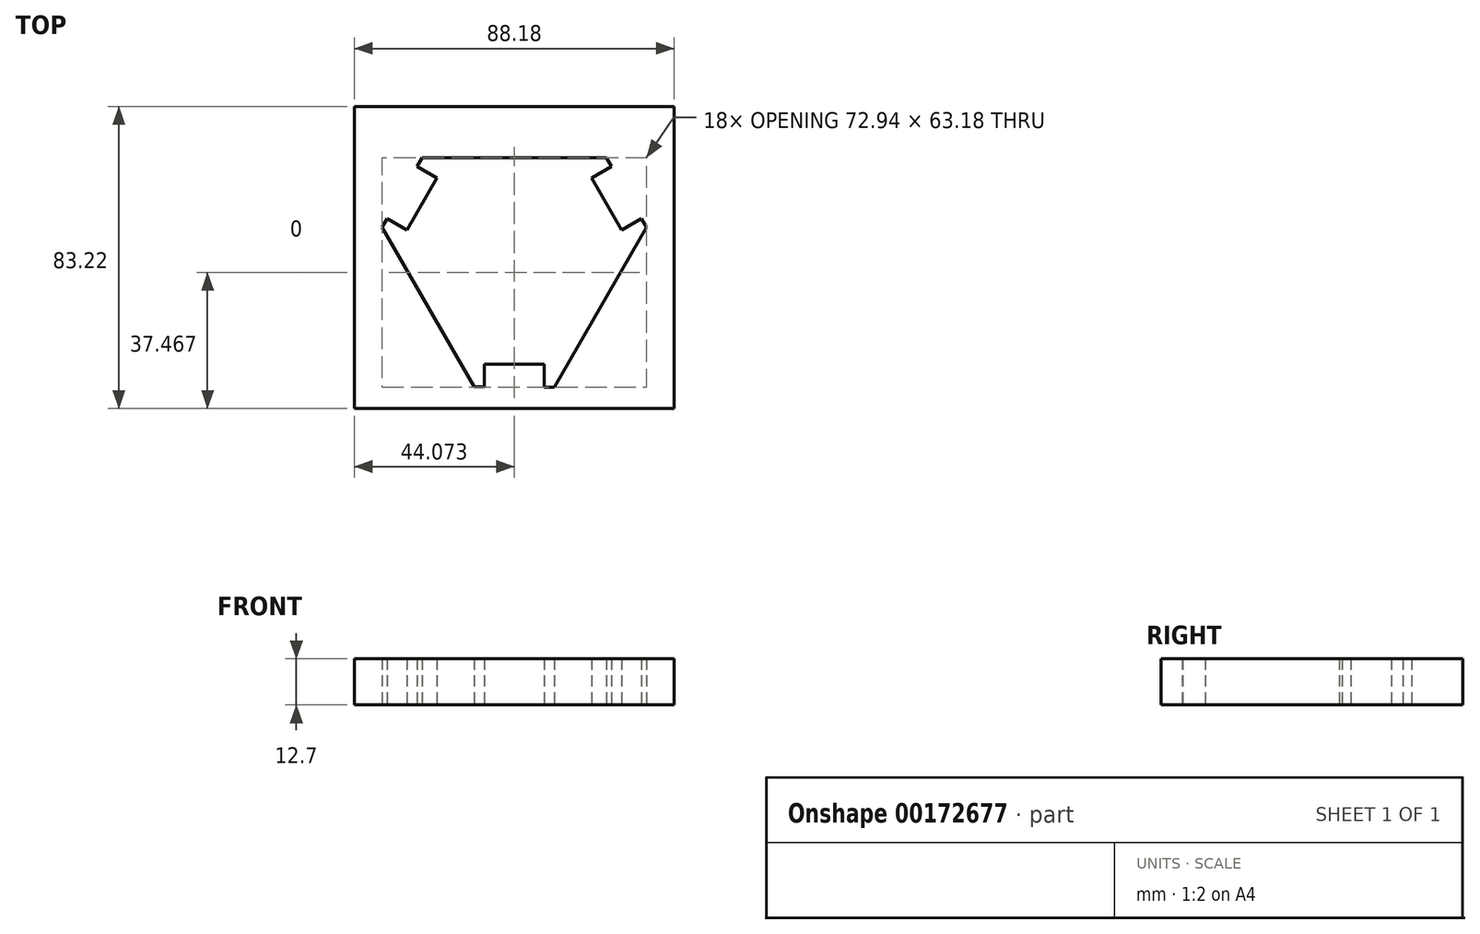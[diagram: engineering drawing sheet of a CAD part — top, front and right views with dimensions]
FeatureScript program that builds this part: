
annotation { "Feature Type Name" : "Feature", "Feature Type Description" : "" }
export const myFeature = defineFeature(function(context is Context, id is Id, definition is map)
    precondition{}
    {
        {
            var Q0;
            Q0=qCreatedBy(makeId("Top.planeOp"),FACE);
            var sketch = newSketch(context, id + "F0", { "sketchPlane" : qUnion([Q0])});
            skCircle(sketch, "E0", {"center": v(0, 0) * mm, "radius": 6.35 * mm, "construction": true});
            skLineSegment(sketch, "E1.bottom", {"start": v(-1.6, 6.15) * mm, "end": v(1.6, 6.15) * mm, "construction": true});
            skLineSegment(sketch, "E1.top", {"start": v(-1.6, 24.25) * mm, "end": v(0, 24.25) * mm, "construction": true});
            skLineSegment(sketch, "E1.left", {"start": v(-1.6, 6.15) * mm, "end": v(-1.6, 24.25) * mm, "construction": true});
            skLineSegment(sketch, "E1.right", {"start": v(1.6, 6.15) * mm, "end": v(1.6, 24.25) * mm, "construction": true});
            skLineSegment(sketch, "E2.bottom", {"start": v(-25.4, 27.45) * mm, "end": v(25.4, 27.45) * mm});
            skLineSegment(sketch, "E2.left", {"start": v(-25.4, 27.45) * mm, "end": v(-25.4, 24.25) * mm, "construction": true});
            skLineSegment(sketch, "E2.right", {"start": v(25.4, 27.45) * mm, "end": v(25.4, 24.25) * mm, "construction": true});
            skPoint(sketch, "E2.middle", {"position": v(0, 24.25) * mm});
            skLineSegment(sketch, "E3", {"start": v(-25.4, 24.25) * mm, "end": v(-1.6, 24.25) * mm, "construction": true});
            skPoint(sketch, "E4.orphan", {"position": v(-25.4, 21.05) * mm});
            skPoint(sketch, "E5.orphan", {"position": v(25.4, 21.05) * mm});
            skLineSegment(sketch, "E6.trimOffspring", {"start": v(1.6, 24.25) * mm, "end": v(25.4, 24.25) * mm, "construction": true});
            skLineSegment(sketch, "E7.1.0", {"start": v(-11.09, -35.7) * mm, "end": v(-36.49, 8.29) * mm});
            skLineSegment(sketch, "E7.1.1", {"start": v(-36.49, 8.29) * mm, "end": v(-33.71, 9.88) * mm, "construction": true});
            skLineSegment(sketch, "E7.1.2", {"start": v(-21.81, -10.73) * mm, "end": v(-33.71, 9.88) * mm, "construction": true});
            skLineSegment(sketch, "E7.1.3", {"start": v(-8.31, -34.11) * mm, "end": v(-20.21, -13.5) * mm, "construction": true});
            skLineSegment(sketch, "E7.1.4", {"start": v(-11.09, -35.7) * mm, "end": v(-8.31, -34.11) * mm, "construction": true});
            skLineSegment(sketch, "E7.1.5", {"start": v(-6.14, -1.68) * mm, "end": v(-21.81, -10.73) * mm, "construction": true});
            skLineSegment(sketch, "E7.1.6", {"start": v(-4.54, -4.45) * mm, "end": v(-20.21, -13.5) * mm, "construction": true});
            skLineSegment(sketch, "E7.2.0", {"start": v(36.45, 8.26) * mm, "end": v(11.05, -35.73) * mm});
            skLineSegment(sketch, "E7.2.1", {"start": v(11.05, -35.73) * mm, "end": v(8.28, -34.13) * mm, "construction": true});
            skLineSegment(sketch, "E7.2.2", {"start": v(20.18, -13.52) * mm, "end": v(8.28, -34.13) * mm, "construction": true});
            skLineSegment(sketch, "E7.2.3", {"start": v(33.68, 9.87) * mm, "end": v(21.78, -10.75) * mm, "construction": true});
            skLineSegment(sketch, "E7.2.4", {"start": v(36.45, 8.26) * mm, "end": v(33.68, 9.87) * mm, "construction": true});
            skLineSegment(sketch, "E7.2.5", {"start": v(4.5, -4.47) * mm, "end": v(20.18, -13.52) * mm, "construction": true});
            skLineSegment(sketch, "E7.2.6", {"start": v(6.1, -1.7) * mm, "end": v(21.78, -10.75) * mm, "construction": true});
            skPoint(sketch, "E7.center", {"position": v(-0.01, 0) * mm});
            skLineSegment(sketch, "E8", {"start": v(-25.4, 27.45) * mm, "end": v(-26.78, 25.05) * mm});
            skLineSegment(sketch, "E9", {"start": v(-11.09, -35.7) * mm, "end": v(-8.31, -35.71) * mm});
            skLineSegment(sketch, "E10", {"start": v(36.45, 8.26) * mm, "end": v(35.08, 10.65) * mm});
            skLineSegment(sketch, "E11.top", {"start": v(-8.31, -29.4) * mm, "end": v(8.28, -29.4) * mm});
            skLineSegment(sketch, "E11.left", {"start": v(-8.31, -35.71) * mm, "end": v(-8.31, -29.4) * mm});
            skLineSegment(sketch, "E11.right", {"start": v(8.28, -35.73) * mm, "end": v(8.28, -29.4) * mm});
            skPoint(sketch, "E12.center", {"position": v(-5.28, -2.42) * mm});
            skLineSegment(sketch, "E13", {"start": v(-26.78, 25.05) * mm, "end": v(-21.3, 21.88) * mm});
            skLineSegment(sketch, "E14.1.0", {"start": v(29.61, 7.5) * mm, "end": v(21.31, 21.87) * mm});
            skLineSegment(sketch, "E14.1.1", {"start": v(35.08, 10.66) * mm, "end": v(29.61, 7.5) * mm});
            skLineSegment(sketch, "E14.1.2", {"start": v(26.8, 25.03) * mm, "end": v(21.31, 21.87) * mm});
            skLineSegment(sketch, "E14.2.0", {"start": v(-21.3, 21.9) * mm, "end": v(-29.6, 7.52) * mm});
            skLineSegment(sketch, "E14.2.1", {"start": v(-26.77, 25.06) * mm, "end": v(-21.3, 21.9) * mm});
            skLineSegment(sketch, "E14.2.2", {"start": v(-35.32, 10.83) * mm, "end": v(-29.6, 7.52) * mm});
            skLineSegment(sketch, "E15.trimOffspring", {"start": v(-35.1, 10.7) * mm, "end": v(-36.49, 8.29) * mm});
            skLineSegment(sketch, "E16.trimOffspring", {"start": v(26.8, 25.03) * mm, "end": v(25.4, 27.45) * mm});
            skLineSegment(sketch, "E17.trimOffspring", {"start": v(8.28, -35.73) * mm, "end": v(11.05, -35.73) * mm});
            skLineSegment(sketch, "E18.bottom", {"start": v(44.1, 41.6) * mm, "end": v(-44.1, 41.6) * mm});
            skLineSegment(sketch, "E18.top", {"start": v(44.1, -41.6) * mm, "end": v(-44.1, -41.6) * mm});
            skLineSegment(sketch, "E18.left", {"start": v(44.1, 41.6) * mm, "end": v(44.1, -41.6) * mm});
            skLineSegment(sketch, "E18.right", {"start": v(-44.1, 41.6) * mm, "end": v(-44.1, -41.6) * mm});
            skPoint(sketch, "E19.orphan", {"position": v(-19.86, 21.05) * mm});
            skPoint(sketch, "E20.orphan", {"position": v(27.04, 25.17) * mm});
            skPoint(sketch, "E21.orphan", {"position": v(8.28, -36) * mm});
            skSolve(sketch);
        }
        {
            var Q0;
            Q0 = qSketchRegion(id + "F0", true);
            extrude(context, id + "F1", {"entities" : qUnion([Q0]), "endBound" : BoundingType.SYMMETRIC, "depth" : 12.7 * mm});
        }
    });
